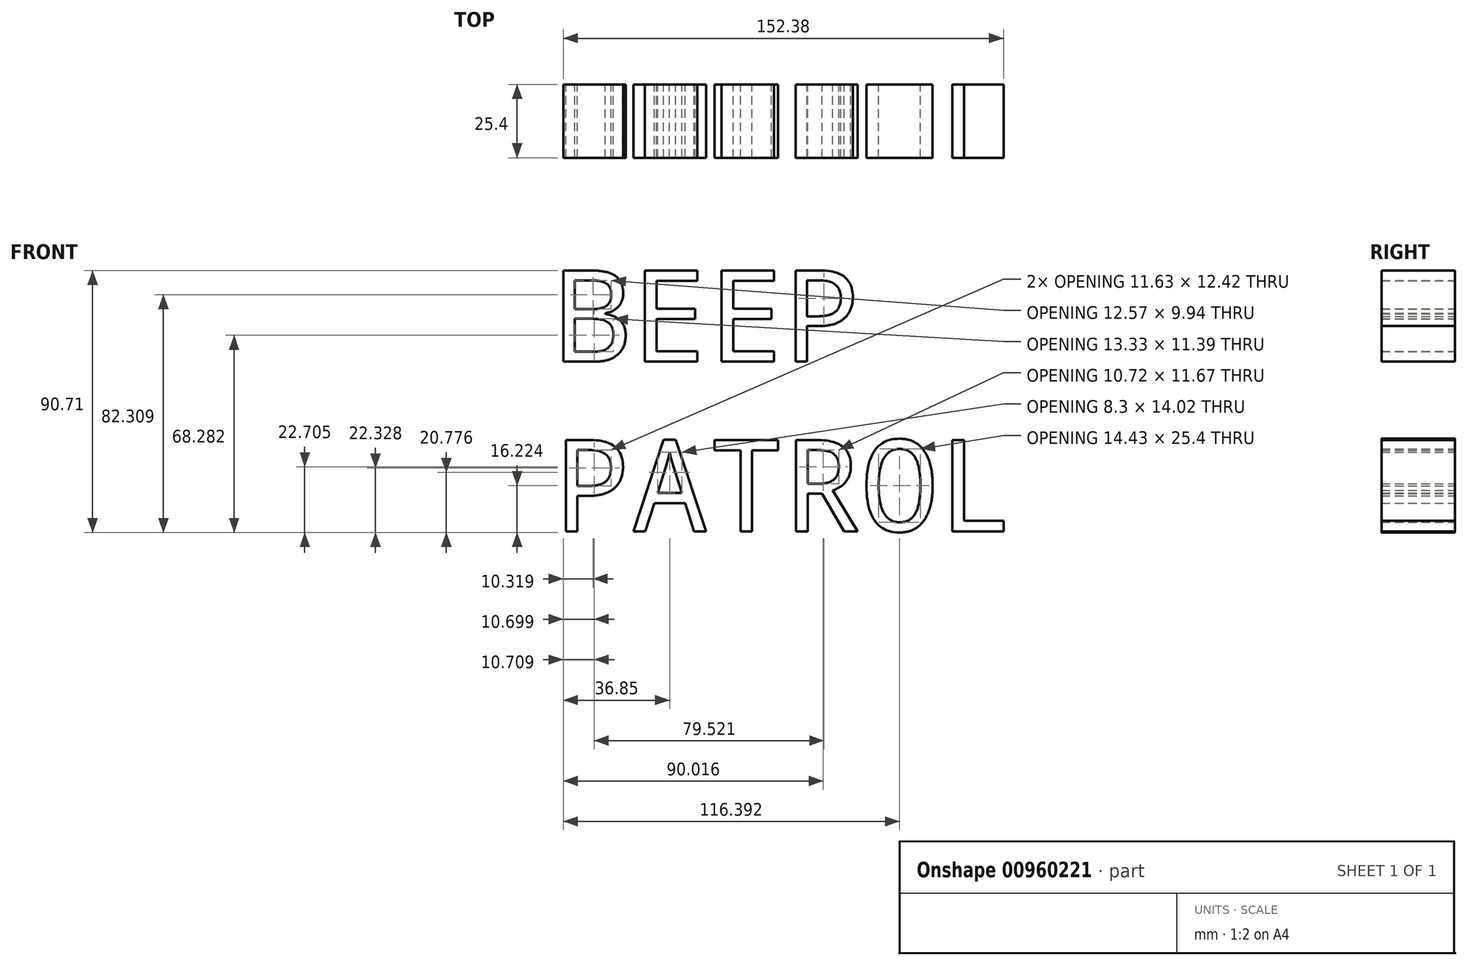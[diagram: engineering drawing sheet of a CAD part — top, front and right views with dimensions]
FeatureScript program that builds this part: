
annotation { "Feature Type Name" : "Feature", "Feature Type Description" : "" }
export const myFeature = defineFeature(function(context is Context, id is Id, definition is map)
    precondition{}
    {
        {
            var Q0;
            Q0=qCreatedBy(makeId("Front.planeOp"),FACE);
            var sketch = newSketch(context, id + "F0", { "sketchPlane" : qUnion([Q0])});
            skText(sketch, "E0", { "text": "BEEP \nPATROL\n", "fontName": "DroidSansMono.ttf"});
            const initialGuessF0  = {"E0": [-0.14296, 0.00663, 1, 0, 0.0318]};
            skSetInitialGuess(sketch, initialGuessF0);
            skSolve(sketch);
        }
        {
            var Q0;
            Q0 = qSketchRegion(id + "F0", true);
            extrude(context, id + "F1", {"entities" : qUnion([Q0]), "depth" : 25.4 * mm, "offsetDistance" : 25.4 * mm});
        }
    });
